# Revit family: 138176861_Mueble Pontus Plus 80 cm con Lavamanos
name_source: partatom
category: Furniture
units: mm (PartAtom-declared; Revit-internal decimal feet)

## family parameters
Always vertical = Yes
Cut with Voids When Loaded = No
OmniClass Number = 23.31.13.11
OmniClass Title = Single Sinks
Room Calculation Point = No
Shared = No
Work Plane-Based = No

## types (1)
- 138176861_Mueble Pontus Plus 80 cm con Lavamanos
    Acabado = Corona_Madera_Onix
    Alto = 764 mm  [stored 2.50656 ft]
    Ancho = 800 mm  [stored 2.62467 ft]
    Carga Máxima = 88,2 lb (40 kg)
    Creado por = IDD
    Description = Linea de Muebles Pontus Plus con acabado de pintura blanca brillante que da
mayor amplitud a los espacios.
· Dos cajones con 30Kg de resistencia.
· Máxima capacidad de almacenamiento.
· Lavamanos 100% en porcelana con superficie amplia de apoyo.
· Resistentes a la humedad.
    Fecha de creación = 05/08/2020
    Garantía = 1 Año  (Madera)
    Garantía Herraje = 1 Año
    Longitud = 450 mm  [stored 1.47638 ft]
    Manufacturer = Corona
    Material = Corona_Madera_Blanco
    Model = Pontus Plus 45
    Peso Bruto aprox = 52,0 lb (23,6 kg).
    Peso Neto aprox = 42,5 lb (19,3 kg).
    Resistencia a la humedad = 8%.

note: [stored X ft] marks values corroborated as IEEE doubles in the binary element streams (Revit-internal decimal feet)

## geometry (parser evidence)
native form markers: Sweep x11
no freeform markers — native parametric forms only
